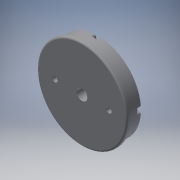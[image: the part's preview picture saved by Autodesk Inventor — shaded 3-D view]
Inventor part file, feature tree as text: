
AUTODESK INVENTOR PART (.ipt)
format: ipt  version: 2018 (Build 220112000, 112)  size: 201,216 bytes
history: native  units: in
note: dims shown in document units (in); Inventor stores cm internally (conversion verified against a paired STEP export)
features: reference x7, extrude x5, sketch x5, other x2, fillet x1, projected_geometry x1
ambient origin geometry x8: Origin, YZ Plane, XZ Plane, XY Plane, X Axis, Y Axis, Z Axis, Center Point
bodies: Solid1 (feature_tree)
feature tree (21):
  extrude  "Extrusion1"  Depth=1.5748in TaperAngle=360.0deg
  extrude  "Extrusion2"  Depth=0.1969in TaperAngle=0.0deg
  extrude  "Extrusion3"  Depth=0.0394in
  fillet  "Fillet1"  Radius=1.5748in
  extrude  "Extrusion4"  Depth=0.2362in
  extrude  "Extrusion5"  Depth=0.1181in
  sketch  "Sketch1"  dims[d0=0.0866in d2=1.5748in d4=360.0deg]
  reference  "Reference1"
  reference  "Reference2"
  reference  "Reference3"
  reference  "Reference4"
  reference  "Reference5"
  sketch  "Sketch2"  dims[d6=0.0787in d7=0.0in d8=0.1969in d9=0.0in]
  projected_geometry  "Projected Loop1"
  sketch  "Sketch3"  dims[d10=0.0787in d11=0.0in d12=0.0394in d13=1.5748in]
  reference  "Reference6"
  sketch  "Sketch4"  dims[d14=0.1969in d15=0.0in d16=0.2362in]
  reference  "Reference7"
  sketch  "Sketch5"  dims[d17=0.1181in d18=0.1181in d19=0.2756in d20=0.0in]
  other  "Assembly1"
  other  "CanSatHousing:1"
